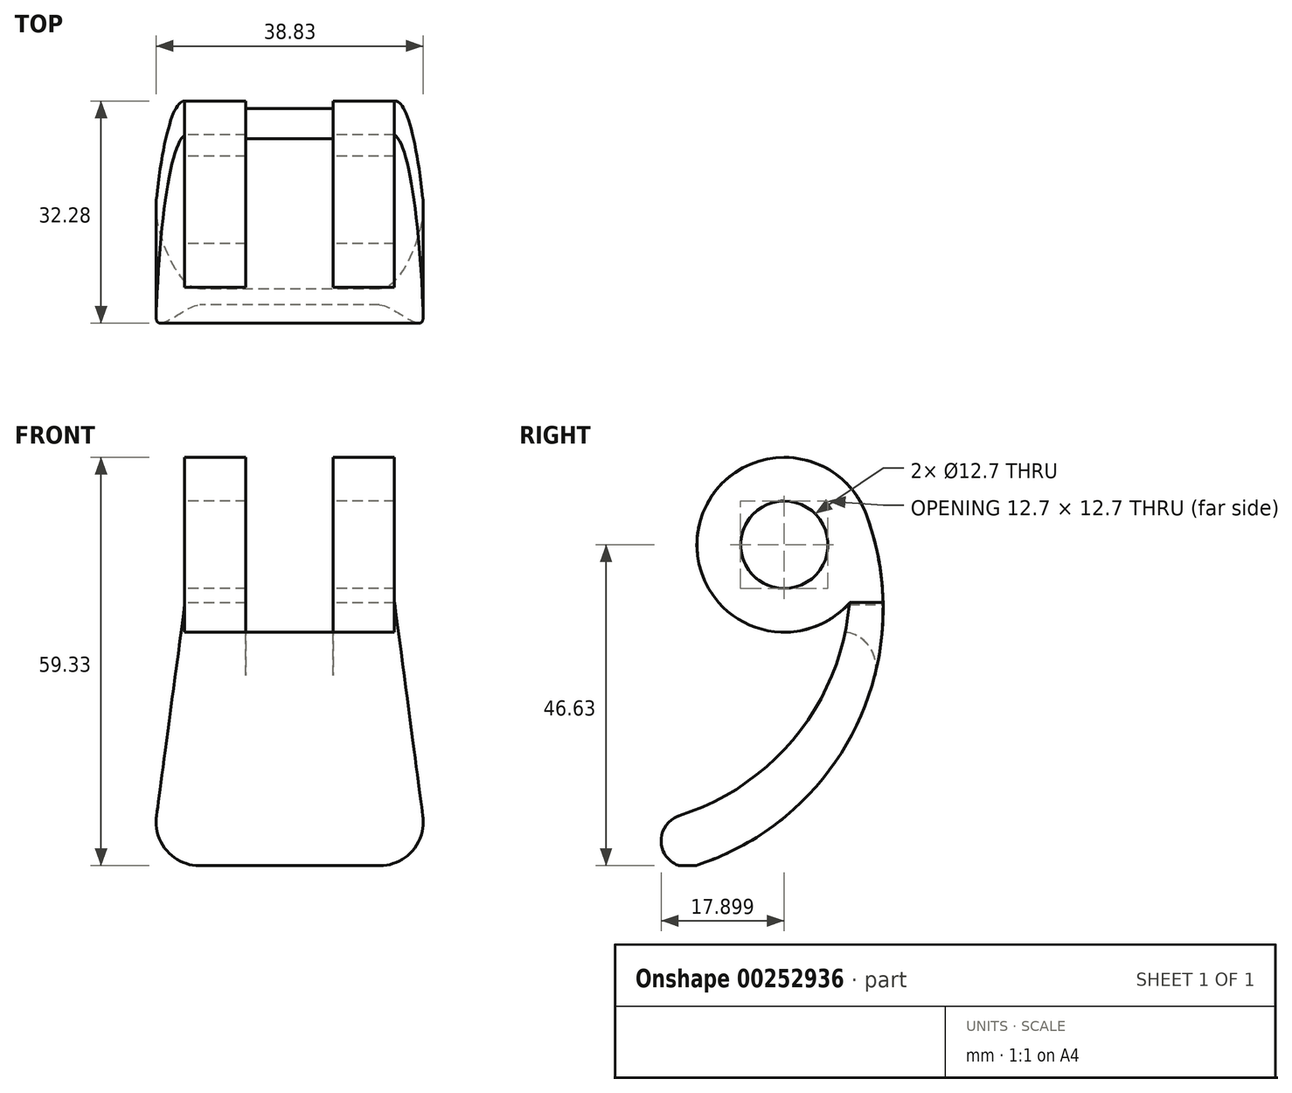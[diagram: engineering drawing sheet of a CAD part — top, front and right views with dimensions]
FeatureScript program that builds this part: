
annotation { "Feature Type Name" : "Feature", "Feature Type Description" : "" }
export const myFeature = defineFeature(function(context is Context, id is Id, definition is map)
    precondition{}
    {
        {
            var Q0;
            Q0=qCreatedBy(makeId("Front.planeOp"),FACE);
            var sketch = newSketch(context, id + "F0", { "sketchPlane" : qUnion([Q0])});
            skCircle(sketch, "E0", {"center": v(0, 0) * mm, "radius": 12.7 * mm});
            skCircle(sketch, "E1", {"center": v(0, 0) * mm, "radius": 6.35 * mm});
            skSolve(sketch);
        }
        {
            var Q0;
            Q0=qSketchRegion(id+"F0",true);
            extrude(context, id + "F1", {"entities" : qUnion([Q0]), "endBound" : BoundingType.SYMMETRIC, "depth" : 30.48 * mm});
        }
        {
            var Q0;
            Q0=qCreatedBy(makeId("Front.planeOp"),FACE);
            var sketch = newSketch(context, id + "F2", { "sketchPlane" : qUnion([Q0])});
            skArc(sketch, "E2", {"start": v(-12.94, -46.63) * mm, "mid": v(10.43, -26.42) * mm, "end": v(11.9, 4.44) * mm});
            skArc(sketch, "E3", {"start": v(-15.24, -39.37) * mm, "mid": v(1.83, -27.66) * mm, "end": v(9.5, -8.43) * mm});
            skArc(sketch, "E4", {"start": v(-15.24, -39.37) * mm, "mid": v(-17.73, -44.15) * mm, "end": v(-12.94, -46.63) * mm});
            skArc(sketch, "E5", {"start": v(9.5, -8.43) * mm, "mid": v(12.48, -2.33) * mm, "end": v(11.9, 4.44) * mm});
            skSolve(sketch);
        }
        {
            var Q0;
            Q0=qSketchRegion(id+"F2",true);
            extrude(context, id + "F3", {"entities" : qUnion([Q0]), "operationType" : NewBodyOperationType.ADD, "endBound" : BoundingType.SYMMETRIC, "depth" : 40.64 * mm});
        }
        {
            var Q0;
            Q0=qCreatedBy(makeId("Front.planeOp"),FACE);
            var sketch = newSketch(context, id + "F4", { "sketchPlane" : qUnion([Q0])});
            skCircle(sketch, "E6", {"center": v(0, 0) * mm, "radius": 12.7 * mm});
            skSolve(sketch);
        }
        {
            var Q0;
            Q0=qSketchRegion(id+"F4",true);
            extrude(context, id + "F5", {"entities" : qUnion([Q0]), "operationType" : NewBodyOperationType.REMOVE, "endBound" : BoundingType.SYMMETRIC, "depth" : 12.7 * mm});
        }
        {
            var Q0;
            Q0=qCreatedBy(makeId("Right.planeOp"),FACE);
            var sketch = newSketch(context, id + "F6", { "sketchPlane" : qUnion([Q0])});
            skLineSegment(sketch, "E7.bottom", {"start": v(-6.35, 12.7) * mm, "end": v(6.35, 12.7) * mm});
            skLineSegment(sketch, "E7.top", {"start": v(-6.35, -12.7) * mm, "end": v(6.35, -12.7) * mm});
            skLineSegment(sketch, "E7.left", {"start": v(-6.35, 12.7) * mm, "end": v(-6.35, -12.7) * mm});
            skLineSegment(sketch, "E7.right", {"start": v(6.35, 12.7) * mm, "end": v(6.35, -12.7) * mm});
            skSolve(sketch);
        }
        {
            var Q0;
            Q0=qSketchRegion(id+"F6",true);
            extrude(context, id + "F7", {"entities" : qUnion([Q0]), "operationType" : NewBodyOperationType.REMOVE, "endBound" : BoundingType.THROUGH_ALL, "depth" : 25.4 * mm});
        }
        {
            var Q0;
            Q0=makeQuery(id+"F7.boolean.opBoolean","INTERSECT",EDGE,{"derivedFrom":[makeQuery(id+"F3.opExtrude","SWEPT_FACE",FACE,{"disambiguationData":[OSD([sQuery(id+"F2.wireOp",EDGE,"E2")])]}),makeQuery(id+"F7.opExtrude","SWEPT_FACE",FACE,{"disambiguationData":[OSD([sQuery(id+"F6.wireOp",EDGE,"E7.top")])]})]});
            fillet(context, id + "F8", {"entities" : qUnion([Q0]), "radius" : 5.08 * mm, "tangentPropagation" : true, "allowEdgeOverflow" : false});
        }
        {
            var Q0;
            Q0=qCreatedBy(makeId("Right.planeOp"),FACE);
            var sketch = newSketch(context, id + "F9", { "sketchPlane" : qUnion([Q0])});
            skLineSegment(sketch, "E8", {"start": v(0, 0) * mm, "end": v(0, 34.87) * mm, "construction": true});
            skSolve(sketch);
        }
        {
            var Q0;
            Q0=makeQuery(id+"F1.opExtrude","SWEPT_BODY",BODY,{"disambiguationData":[OSD([sQuery(id+"F0.wireOp",EDGE,"E0"),sQuery(id+"F0.wireOp",EDGE,"E1")])]});
            var Q1;
            Q1=sQuery(id+"F9.wireOp",EDGE,"E8");
            transform(context, id + "F10", {"entities" : qUnion([Q0]), "transformType" : TransformType.ROTATION, "transformAxis" : qUnion([Q1]), "angle" : 1.57 * radian, "makeCopy" : false});
        }
        {
            var Q0;
            Q0=qCreatedBy(makeId("Front.planeOp"),FACE);
            var sketch = newSketch(context, id + "F11", { "sketchPlane" : qUnion([Q0])});
            skLineSegment(sketch, "E9", {"start": v(15.24, -8.38) * mm, "end": v(19.37, -39.45) * mm});
            skLineSegment(sketch, "E10", {"start": v(13.07, -46.63) * mm, "end": v(-13.06, -46.63) * mm});
            skLineSegment(sketch, "E11", {"start": v(-19.36, -39.44) * mm, "end": v(-15.24, -8.7) * mm});
            skLineSegment(sketch, "E12", {"start": v(-15.24, -8.7) * mm, "end": v(-15.24, 12.7) * mm});
            skLineSegment(sketch, "E13", {"start": v(-15.24, 12.7) * mm, "end": v(15.24, 12.7) * mm});
            skLineSegment(sketch, "E14", {"start": v(15.24, 12.7) * mm, "end": v(15.24, -8.38) * mm});
            skPoint(sketch, "E15.visualSharp", {"position": v(20.32, -46.63) * mm});
            skArc(sketch, "E15.filletArc", {"start": v(13.07, -46.63) * mm, "mid": v(17.85, -44.47) * mm, "end": v(19.37, -39.45) * mm});
            skPoint(sketch, "E16.visualSharp", {"position": v(-20.32, -46.63) * mm});
            skArc(sketch, "E16.filletArc", {"start": v(-19.36, -39.44) * mm, "mid": v(-17.84, -44.47) * mm, "end": v(-13.06, -46.63) * mm});
            skSolve(sketch);
        }
        {
            var Q0;
            Q0 = qSketchRegion(id + "F11", true);
            extrude(context, id + "F12", {"entities" : qUnion([Q0]), "operationType" : NewBodyOperationType.INTERSECT, "endBound" : BoundingType.SYMMETRIC, "depth" : 76.2 * mm});
        }
    });
